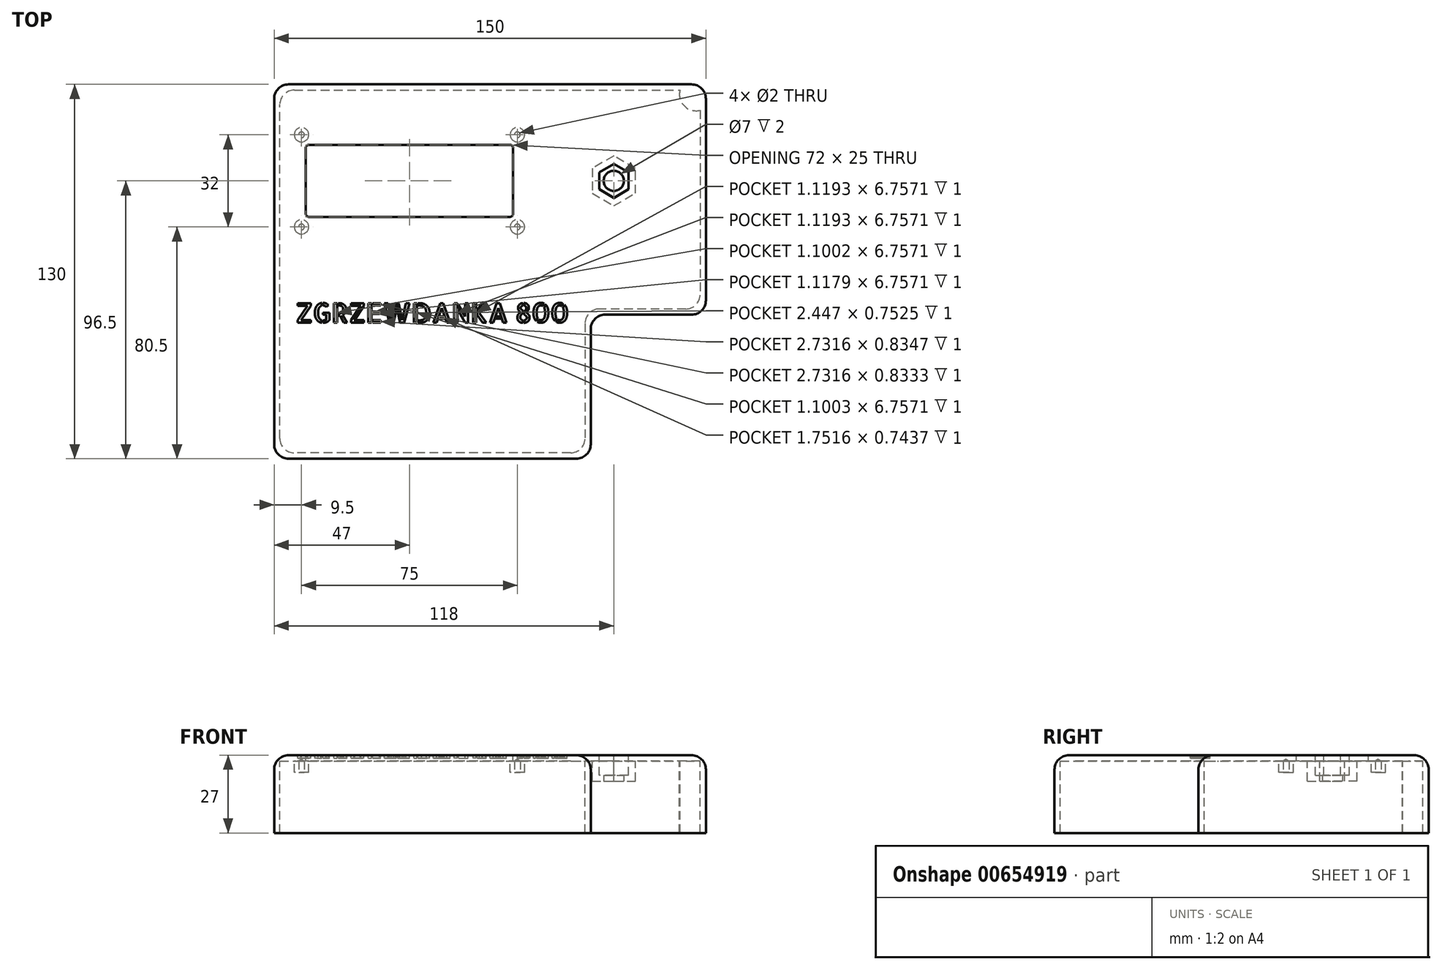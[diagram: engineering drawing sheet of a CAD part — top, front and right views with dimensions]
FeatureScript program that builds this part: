
annotation { "Feature Type Name" : "Feature", "Feature Type Description" : "" }
export const myFeature = defineFeature(function(context is Context, id is Id, definition is map)
    precondition{}
    {
        {
            var Q0;
            Q0=qCreatedBy(makeId("Top.planeOp"),FACE);
            var sketch = newSketch(context, id + "F0", { "sketchPlane" : qUnion([Q0])});
            skLineSegment(sketch, "E0", {"start": v(0, 0) * mm, "end": v(0, 130) * mm});
            skLineSegment(sketch, "E1", {"start": v(0, 130) * mm, "end": v(150, 130) * mm});
            skLineSegment(sketch, "E2", {"start": v(150, 130) * mm, "end": v(150, 50) * mm});
            skLineSegment(sketch, "E3", {"start": v(150, 50) * mm, "end": v(110, 50) * mm});
            skLineSegment(sketch, "E4", {"start": v(110, 50) * mm, "end": v(110, 0) * mm});
            skLineSegment(sketch, "E5", {"start": v(110, 0) * mm, "end": v(0, 0) * mm});
            skSolve(sketch);
        }
        {
            var Q0;
            Q0=makeQuery(id+"F0.imprint","IMPRINT",FACE,{"disambiguationData":[TD([[makeQuery(id+"F0.imprint","IMPRINT",EDGE,{"derivedFrom":sQuery(id+"F0.wireOp",EDGE,"E0")}),-1.0]])]});
            extrude(context, id + "F1", {"entities" : qUnion([Q0]), "depth" : 2 * mm, "offsetDistance" : 25 * mm});
        }
        {
            var Q0;
            Q0=makeQuery(id+"F1.opExtrude","CAP_FACE",FACE,{"disambiguationData":[OSD([sQuery(id+"F0.wireOp",EDGE,"E0"),sQuery(id+"F0.wireOp",EDGE,"E1"),sQuery(id+"F0.wireOp",EDGE,"E2"),sQuery(id+"F0.wireOp",EDGE,"E3"),sQuery(id+"F0.wireOp",EDGE,"E4"),sQuery(id+"F0.wireOp",EDGE,"E5")])],"isStart":false});
            var sketch = newSketch(context, id + "F2", { "sketchPlane" : qUnion([Q0])});
            skLineSegment(sketch, "E6.bottom", {"start": v(11, 109) * mm, "end": v(83, 109) * mm});
            skLineSegment(sketch, "E6.top", {"start": v(11, 84) * mm, "end": v(83, 84) * mm});
            skLineSegment(sketch, "E6.left", {"start": v(11, 109) * mm, "end": v(11, 84) * mm});
            skLineSegment(sketch, "E6.right", {"start": v(83, 109) * mm, "end": v(83, 84) * mm});
            skSolve(sketch);
        }
        {
            var Q0;
            Q0 = qSketchRegion(id + "F2", true);
            extrude(context, id + "F3", {"entities" : qUnion([Q0]), "operationType" : NewBodyOperationType.REMOVE, "oppositeDirection" : true, "depth" : 7 * mm, "offsetDistance" : 25 * mm});
        }
        {
            var Q0;
            Q0=makeQuery(id+"F1.opExtrude","CAP_FACE",FACE,{"disambiguationData":[OSD([sQuery(id+"F0.wireOp",EDGE,"E0"),sQuery(id+"F0.wireOp",EDGE,"E1"),sQuery(id+"F0.wireOp",EDGE,"E2"),sQuery(id+"F0.wireOp",EDGE,"E3"),sQuery(id+"F0.wireOp",EDGE,"E4"),sQuery(id+"F0.wireOp",EDGE,"E5")])],"isStart":true});
            var sketch = newSketch(context, id + "F4", { "sketchPlane" : qUnion([Q0])});
            skLineSegment(sketch, "E7", {"start": v(110, 0) * mm, "end": v(0, 0) * mm});
            skLineSegment(sketch, "E8", {"start": v(0, 0) * mm, "end": v(0, -130) * mm});
            skLineSegment(sketch, "E9", {"start": v(0, -130) * mm, "end": v(150, -130) * mm});
            skLineSegment(sketch, "E10", {"start": v(150, -130) * mm, "end": v(150, -50) * mm});
            skLineSegment(sketch, "E11", {"start": v(150, -50) * mm, "end": v(110, -50) * mm});
            skLineSegment(sketch, "E12", {"start": v(110, -50) * mm, "end": v(110, 0) * mm});
            skLineSegment(sketch, "E13", {"start": v(148, -52) * mm, "end": v(108, -52) * mm});
            skLineSegment(sketch, "E14", {"start": v(108, -52) * mm, "end": v(108, -2) * mm});
            skLineSegment(sketch, "E15", {"start": v(108, -2) * mm, "end": v(2, -2) * mm});
            skLineSegment(sketch, "E16", {"start": v(2, -2) * mm, "end": v(2, -128) * mm});
            skLineSegment(sketch, "E17", {"start": v(2, -128) * mm, "end": v(148, -128) * mm});
            skLineSegment(sketch, "E18", {"start": v(148, -128) * mm, "end": v(148, -52) * mm});
            skSolve(sketch);
        }
        {
            var Q0;
            Q0 = qSketchRegion(id + "F4", true);
            extrude(context, id + "F5", {"entities" : qUnion([Q0]), "operationType" : NewBodyOperationType.ADD, "depth" : 25 * mm, "offsetDistance" : 25 * mm});
        }
        {
            var Q0;
            Q0=makeQuery(id+"F5.boolean.opBoolean","MERGE",EDGE,{"derivedFrom":[makeQuery(id+"F1.opExtrude","SWEPT_EDGE",EDGE,{"disambiguationData":[OSD([sQuery(id+"F0.wireOp",EDGE,"E4"),sQuery(id+"F0.wireOp",EDGE,"E5")])]}),makeQuery(id+"F5.opExtrude","SWEPT_EDGE",EDGE,{"disambiguationData":[OSD([sQuery(id+"F4.wireOp",EDGE,"E7"),sQuery(id+"F4.wireOp",EDGE,"E12")])]})]});
            fillet(context, id + "F6", {"entities" : qUnion([Q0]), "radius" : 5 * mm, "tangentPropagation" : true, "allowEdgeOverflow" : false});
        }
        {
            var Q0;
            Q0=makeQuery(id+"F1.opExtrude","CAP_FACE",FACE,{"disambiguationData":[OSD([sQuery(id+"F0.wireOp",EDGE,"E0"),sQuery(id+"F0.wireOp",EDGE,"E1"),sQuery(id+"F0.wireOp",EDGE,"E2"),sQuery(id+"F0.wireOp",EDGE,"E3"),sQuery(id+"F0.wireOp",EDGE,"E4"),sQuery(id+"F0.wireOp",EDGE,"E5")])],"isStart":true});
            var sketch = newSketch(context, id + "F7", { "sketchPlane" : qUnion([Q0])});
            skPoint(sketch, "E19", {"position": v(84.5, -112.5) * mm});
            skPoint(sketch, "E20", {"position": v(84.5, -80.5) * mm});
            skPoint(sketch, "E21", {"position": v(9.5, -112.5) * mm});
            skPoint(sketch, "E22", {"position": v(9.5, -80.5) * mm});
            skCircle(sketch, "E23", {"center": v(84.5, -112.5) * mm, "radius": 2.5 * mm});
            skCircle(sketch, "E24", {"center": v(9.5, -112.5) * mm, "radius": 2.5 * mm});
            skCircle(sketch, "E25", {"center": v(9.5, -80.5) * mm, "radius": 2.5 * mm});
            skCircle(sketch, "E26", {"center": v(84.5, -80.5) * mm, "radius": 2.5 * mm});
            skLineSegment(sketch, "E27", {"start": v(11, -96.5) * mm, "end": v(83, -96.5) * mm});
            skLineSegment(sketch, "E28", {"start": v(47, -109) * mm, "end": v(47, -84) * mm});
            skSolve(sketch);
        }
        {
            var Q0;
            Q0=makeQuery(id+"F3.boolean.opBoolean","COPY",EDGE,{"derivedFrom":makeQuery(id+"F3.opExtrude","SWEPT_EDGE",EDGE,{"disambiguationData":[OSD([sQuery(id+"F2.wireOp",EDGE,"E6.bottom"),sQuery(id+"F2.wireOp",EDGE,"E6.right")])]})});
            var Q1;
            Q1=makeQuery(id+"F3.boolean.opBoolean","COPY",EDGE,{"derivedFrom":makeQuery(id+"F3.opExtrude","SWEPT_EDGE",EDGE,{"disambiguationData":[OSD([sQuery(id+"F2.wireOp",EDGE,"E6.top"),sQuery(id+"F2.wireOp",EDGE,"E6.right")])]})});
            var Q2;
            Q2=makeQuery(id+"F3.boolean.opBoolean","COPY",EDGE,{"derivedFrom":makeQuery(id+"F3.opExtrude","SWEPT_EDGE",EDGE,{"disambiguationData":[OSD([sQuery(id+"F2.wireOp",EDGE,"E6.top"),sQuery(id+"F2.wireOp",EDGE,"E6.left")])]})});
            var Q3;
            Q3=makeQuery(id+"F3.boolean.opBoolean","COPY",EDGE,{"derivedFrom":makeQuery(id+"F3.opExtrude","SWEPT_EDGE",EDGE,{"disambiguationData":[OSD([sQuery(id+"F2.wireOp",EDGE,"E6.bottom"),sQuery(id+"F2.wireOp",EDGE,"E6.left")])]})});
            fillet(context, id + "F8", {"entities" : qUnion([Q0, Q1, Q2, Q3]), "radius" : 1 * mm, "tangentPropagation" : true, "allowEdgeOverflow" : false});
        }
        {
            var Q0;
            Q0=makeQuery(id+"F5.boolean.opBoolean","MERGE",EDGE,{"derivedFrom":[makeQuery(id+"F1.opExtrude","SWEPT_EDGE",EDGE,{"disambiguationData":[OSD([sQuery(id+"F0.wireOp",EDGE,"E0"),sQuery(id+"F0.wireOp",EDGE,"E1")])]}),makeQuery(id+"F5.opExtrude","SWEPT_EDGE",EDGE,{"disambiguationData":[OSD([sQuery(id+"F4.wireOp",EDGE,"E8"),sQuery(id+"F4.wireOp",EDGE,"E9")])]})]});
            var Q1;
            Q1=makeQuery(id+"F5.boolean.opBoolean","MERGE",EDGE,{"derivedFrom":[makeQuery(id+"F1.opExtrude","SWEPT_EDGE",EDGE,{"disambiguationData":[OSD([sQuery(id+"F0.wireOp",EDGE,"E0"),sQuery(id+"F0.wireOp",EDGE,"E5")])]}),makeQuery(id+"F5.opExtrude","SWEPT_EDGE",EDGE,{"disambiguationData":[OSD([sQuery(id+"F4.wireOp",EDGE,"E7"),sQuery(id+"F4.wireOp",EDGE,"E8")])]})]});
            var Q2;
            Q2=makeQuery(id+"F5.boolean.opBoolean","MERGE",EDGE,{"derivedFrom":[makeQuery(id+"F1.opExtrude","SWEPT_EDGE",EDGE,{"disambiguationData":[OSD([sQuery(id+"F0.wireOp",EDGE,"E2"),sQuery(id+"F0.wireOp",EDGE,"E3")])]}),makeQuery(id+"F5.opExtrude","SWEPT_EDGE",EDGE,{"disambiguationData":[OSD([sQuery(id+"F4.wireOp",EDGE,"E10"),sQuery(id+"F4.wireOp",EDGE,"E11")])]})]});
            var Q3;
            Q3=makeQuery(id+"F5.boolean.opBoolean","MERGE",EDGE,{"derivedFrom":[makeQuery(id+"F1.opExtrude","SWEPT_EDGE",EDGE,{"disambiguationData":[OSD([sQuery(id+"F0.wireOp",EDGE,"E3"),sQuery(id+"F0.wireOp",EDGE,"E4")])]}),makeQuery(id+"F5.opExtrude","SWEPT_EDGE",EDGE,{"disambiguationData":[OSD([sQuery(id+"F4.wireOp",EDGE,"E11"),sQuery(id+"F4.wireOp",EDGE,"E12")])]})]});
            var Q4;
            Q4=makeQuery(id+"F5.boolean.opBoolean","MERGE",EDGE,{"derivedFrom":[makeQuery(id+"F1.opExtrude","SWEPT_EDGE",EDGE,{"disambiguationData":[OSD([sQuery(id+"F0.wireOp",EDGE,"E1"),sQuery(id+"F0.wireOp",EDGE,"E2")])]}),makeQuery(id+"F5.opExtrude","SWEPT_EDGE",EDGE,{"disambiguationData":[OSD([sQuery(id+"F4.wireOp",EDGE,"E9"),sQuery(id+"F4.wireOp",EDGE,"E10")])]})]});
            fillet(context, id + "F9", {"entities" : qUnion([Q0, Q1, Q2, Q3, Q4]), "radius" : 5 * mm, "tangentPropagation" : true, "allowEdgeOverflow" : false});
        }
        {
            var Q0;
            Q0=makeQuery(id+"F5.opExtrude","SWEPT_EDGE",EDGE,{"disambiguationData":[OSD([sQuery(id+"F4.wireOp",EDGE,"E13"),sQuery(id+"F4.wireOp",EDGE,"E18")])]});
            var Q1;
            Q1=makeQuery(id+"F5.opExtrude","SWEPT_EDGE",EDGE,{"disambiguationData":[OSD([sQuery(id+"F4.wireOp",EDGE,"E17"),sQuery(id+"F4.wireOp",EDGE,"E18")])]});
            var Q2;
            Q2=makeQuery(id+"F5.opExtrude","SWEPT_EDGE",EDGE,{"disambiguationData":[OSD([sQuery(id+"F4.wireOp",EDGE,"E16"),sQuery(id+"F4.wireOp",EDGE,"E17")])]});
            var Q3;
            Q3=makeQuery(id+"F5.opExtrude","SWEPT_EDGE",EDGE,{"disambiguationData":[OSD([sQuery(id+"F4.wireOp",EDGE,"E14"),sQuery(id+"F4.wireOp",EDGE,"E15")])]});
            var Q4;
            Q4=makeQuery(id+"F5.opExtrude","SWEPT_EDGE",EDGE,{"disambiguationData":[OSD([sQuery(id+"F4.wireOp",EDGE,"E15"),sQuery(id+"F4.wireOp",EDGE,"E16")])]});
            var Q5;
            Q5=makeQuery(id+"F5.opExtrude","SWEPT_EDGE",EDGE,{"disambiguationData":[OSD([sQuery(id+"F4.wireOp",EDGE,"E13"),sQuery(id+"F4.wireOp",EDGE,"E14")])]});
            fillet(context, id + "F10", {"entities" : qUnion([Q0, Q1, Q2, Q3, Q4, Q5]), "radius" : 5 * mm, "tangentPropagation" : true, "allowEdgeOverflow" : false});
        }
        {
            var Q0;
            Q0=makeQuery(id+"F1.opExtrude","CAP_EDGE",EDGE,{"disambiguationData":[OSD([sQuery(id+"F0.wireOp",EDGE,"E0")])],"isStart":false});
            fillet(context, id + "F11", {"entities" : qUnion([Q0]), "radius" : 5 * mm, "tangentPropagation" : true, "allowEdgeOverflow" : false});
        }
        {
            var Q0;
            Q0 = qSketchRegion(id + "F7", true);
            extrude(context, id + "F12", {"entities" : qUnion([Q0]), "operationType" : NewBodyOperationType.ADD, "depth" : 4 * mm, "offsetDistance" : 25 * mm});
        }
        {
            var Q0;
            Q0=makeQuery(id+"F1.opExtrude","CAP_FACE",FACE,{"disambiguationData":[OSD([sQuery(id+"F0.wireOp",EDGE,"E0"),sQuery(id+"F0.wireOp",EDGE,"E1"),sQuery(id+"F0.wireOp",EDGE,"E2"),sQuery(id+"F0.wireOp",EDGE,"E3"),sQuery(id+"F0.wireOp",EDGE,"E4"),sQuery(id+"F0.wireOp",EDGE,"E5")])],"isStart":true});
            var sketch = newSketch(context, id + "F13", { "sketchPlane" : qUnion([Q0])});
            skLineSegment(sketch, "E29", {"start": v(83, -96.5) * mm, "end": v(167.66, -96.5) * mm});
            skPoint(sketch, "E30", {"position": v(118, -96.5) * mm});
            skCircle(sketch, "E31.cCircle", {"center": v(118, -96.5) * mm, "radius": 7.5 * mm, "construction": true});
            skLineSegment(sketch, "E31.0", {"start": v(110.5, -100.83) * mm, "end": v(110.5, -92.17) * mm});
            skLineSegment(sketch, "E31.1", {"start": v(110.5, -92.17) * mm, "end": v(118, -87.84) * mm});
            skLineSegment(sketch, "E31.2", {"start": v(118, -87.84) * mm, "end": v(125.5, -92.17) * mm});
            skLineSegment(sketch, "E31.3", {"start": v(125.5, -92.17) * mm, "end": v(125.5, -100.83) * mm});
            skLineSegment(sketch, "E31.4", {"start": v(125.5, -100.83) * mm, "end": v(118, -105.16) * mm});
            skLineSegment(sketch, "E31.5", {"start": v(118, -105.16) * mm, "end": v(110.5, -100.83) * mm});
            skPoint(sketch, "E31.0.midPoint", {"position": v(110.5, -96.5) * mm});
            skSolve(sketch);
        }
        {
            var Q0;
            Q0 = qSketchRegion(id + "F13", true);
            extrude(context, id + "F14", {"entities" : qUnion([Q0]), "operationType" : NewBodyOperationType.ADD, "depth" : 7 * mm, "offsetDistance" : 25 * mm});
        }
        {
            var Q0;
            Q0=makeQuery(id+"F1.opExtrude","CAP_FACE",FACE,{"disambiguationData":[OSD([sQuery(id+"F0.wireOp",EDGE,"E0"),sQuery(id+"F0.wireOp",EDGE,"E1"),sQuery(id+"F0.wireOp",EDGE,"E2"),sQuery(id+"F0.wireOp",EDGE,"E3"),sQuery(id+"F0.wireOp",EDGE,"E4"),sQuery(id+"F0.wireOp",EDGE,"E5")])],"isStart":true});
            var sketch = newSketch(context, id + "F15", { "sketchPlane" : qUnion([Q0])});
            skLineSegment(sketch, "E32", {"start": v(110.5, -96.5) * mm, "end": v(125.5, -96.5) * mm});
            skCircle(sketch, "E33.cCircle", {"center": v(118, -96.5) * mm, "radius": 5.1 * mm, "construction": true});
            skLineSegment(sketch, "E33.0", {"start": v(123.1, -93.56) * mm, "end": v(123.1, -99.44) * mm});
            skLineSegment(sketch, "E33.1", {"start": v(123.1, -99.44) * mm, "end": v(118, -102.39) * mm});
            skLineSegment(sketch, "E33.2", {"start": v(118, -102.39) * mm, "end": v(112.9, -99.44) * mm});
            skLineSegment(sketch, "E33.3", {"start": v(112.9, -99.44) * mm, "end": v(112.9, -93.56) * mm});
            skLineSegment(sketch, "E33.4", {"start": v(112.9, -93.56) * mm, "end": v(118, -90.61) * mm});
            skLineSegment(sketch, "E33.5", {"start": v(118, -90.61) * mm, "end": v(123.1, -93.56) * mm});
            skPoint(sketch, "E33.0.midPoint", {"position": v(123.1, -96.5) * mm});
            skSolve(sketch);
        }
        {
            var Q0;
            Q0 = qSketchRegion(id + "F15", true);
            extrude(context, id + "F16", {"entities" : qUnion([Q0]), "operationType" : NewBodyOperationType.REMOVE, "depth" : 5 * mm, "offsetDistance" : 25 * mm, "hasSecondDirection" : true, "secondDirectionOppositeDirection" : true, "secondDirectionDepth" : 3 * mm});
        }
        {
            var Q0;
            Q0=makeQuery(id+"F14.opExtrude","CAP_FACE",FACE,{"disambiguationData":[OSD([sQuery(id+"F13.wireOp",EDGE,"E31.0"),sQuery(id+"F13.wireOp",EDGE,"E31.1"),sQuery(id+"F13.wireOp",EDGE,"E31.2"),sQuery(id+"F13.wireOp",EDGE,"E31.3"),sQuery(id+"F13.wireOp",EDGE,"E31.4"),sQuery(id+"F13.wireOp",EDGE,"E31.5")])],"isStart":false});
            var sketch = newSketch(context, id + "F17", { "sketchPlane" : qUnion([Q0])});
            skLineSegment(sketch, "E34", {"start": v(125.5, -96.5) * mm, "end": v(110.5, -96.5) * mm});
            skPoint(sketch, "E35", {"position": v(118, -96.5) * mm});
            skSolve(sketch);
        }
        {
            var Q0;
            Q0=sQuery(id+"F17.wireOp",VERTEX,"E35");
            var Q1;
            Q1=makeQuery(id+"F1.opExtrude","SWEPT_BODY",BODY,{"disambiguationData":[OSD([sQuery(id+"F0.wireOp",EDGE,"E0"),sQuery(id+"F0.wireOp",EDGE,"E1"),sQuery(id+"F0.wireOp",EDGE,"E2"),sQuery(id+"F0.wireOp",EDGE,"E3"),sQuery(id+"F0.wireOp",EDGE,"E4"),sQuery(id+"F0.wireOp",EDGE,"E5")])]});
            hole(context, id + "F18", {"style" : HoleStyle.SIMPLE, "endStyle" : HoleEndStyle.THROUGH, "holeDiameter" : 7 * mm, "majorDiameter" : 5 * mm, "isTappedThrough" : true, "tappedDepth" : 12 * mm, "tapClearance" : 3, "locations" : qUnion([Q0]), "scope" : qUnion([Q1])});
        }
        {
            var Q0;
            Q0=makeQuery(id+"F12.opExtrude","CAP_FACE",FACE,{"disambiguationData":[OSD([sQuery(id+"F7.wireOp",EDGE,"E23")])],"isStart":false});
            var sketch = newSketch(context, id + "F19", { "sketchPlane" : qUnion([Q0])});
            skPoint(sketch, "E36", {"position": v(84.5, -112.5) * mm});
            skSolve(sketch);
        }
        {
            var Q0;
            Q0=makeQuery(id+"F12.opExtrude","CAP_FACE",FACE,{"disambiguationData":[OSD([sQuery(id+"F7.wireOp",EDGE,"E25")])],"isStart":false});
            var sketch = newSketch(context, id + "F20", { "sketchPlane" : qUnion([Q0])});
            skPoint(sketch, "E37", {"position": v(9.5, -80.5) * mm});
            skSolve(sketch);
        }
        {
            var Q0;
            Q0=makeQuery(id+"F12.opExtrude","CAP_FACE",FACE,{"disambiguationData":[OSD([sQuery(id+"F7.wireOp",EDGE,"E26")])],"isStart":false});
            var sketch = newSketch(context, id + "F21", { "sketchPlane" : qUnion([Q0])});
            skPoint(sketch, "E38", {"position": v(84.5, -80.5) * mm});
            skSolve(sketch);
        }
        {
            var Q0;
            Q0=makeQuery(id+"F12.opExtrude","CAP_FACE",FACE,{"disambiguationData":[OSD([sQuery(id+"F7.wireOp",EDGE,"E24")])],"isStart":false});
            var sketch = newSketch(context, id + "F22", { "sketchPlane" : qUnion([Q0])});
            skPoint(sketch, "E39", {"position": v(9.5, -112.5) * mm});
            skSolve(sketch);
        }
        {
            var Q0;
            Q0=sQuery(id+"F22.wireOp",VERTEX,"E39");
            var Q1;
            Q1=sQuery(id+"F20.wireOp",VERTEX,"E37");
            var Q2;
            Q2=sQuery(id+"F21.wireOp",VERTEX,"E38");
            var Q3;
            Q3=sQuery(id+"F19.wireOp",VERTEX,"E36");
            var Q4;
            Q4=makeQuery(id+"F1.opExtrude","SWEPT_BODY",BODY,{"disambiguationData":[OSD([sQuery(id+"F0.wireOp",EDGE,"E0"),sQuery(id+"F0.wireOp",EDGE,"E1"),sQuery(id+"F0.wireOp",EDGE,"E2"),sQuery(id+"F0.wireOp",EDGE,"E3"),sQuery(id+"F0.wireOp",EDGE,"E4"),sQuery(id+"F0.wireOp",EDGE,"E5")])]});
            hole(context, id + "F23", {"style" : HoleStyle.SIMPLE, "endStyle" : HoleEndStyle.BLIND, "holeDiameter" : 2 * mm, "majorDiameter" : 5 * mm, "holeDepth" : 4 * mm, "isTappedThrough" : true, "tappedDepth" : 12 * mm, "tapClearance" : 3, "locations" : qUnion([Q0, Q1, Q2, Q3]), "scope" : qUnion([Q4])});
        }
        {
            var Q0;
            Q0=makeQuery(id+"F2.imprint","IMPRINT",FACE,{"disambiguationData":[TD([[makeQuery(id+"F2.imprint","IMPRINT",EDGE,{"derivedFrom":sQuery(id+"F2.wireOp",EDGE,"E6.bottom")}),1.0]])]});
            var sketch = newSketch(context, id + "F24", { "sketchPlane" : qUnion([Q0])});
            skText(sketch, "E40", { "text": "ZGRZEWDANKA 800", "fontName": "AllertaStencil-Regular.ttf"});
            const initialGuessF24  = {"E40": [0.00749, 0.04725, 1, 0, 0.00676]};
            skSetInitialGuess(sketch, initialGuessF24);
            skSolve(sketch);
        }
        {
            var Q0;
            Q0 = qSketchRegion(id + "F24", true);
            extrude(context, id + "F25", {"entities" : qUnion([Q0]), "operationType" : NewBodyOperationType.REMOVE, "depth" : -1 * mm, "offsetDistance" : 25 * mm});
        }
        {
            var Q0;
            Q0=makeQuery(id+"F1.opExtrude","CAP_FACE",FACE,{"disambiguationData":[OSD([sQuery(id+"F0.wireOp",EDGE,"E0"),sQuery(id+"F0.wireOp",EDGE,"E1"),sQuery(id+"F0.wireOp",EDGE,"E2"),sQuery(id+"F0.wireOp",EDGE,"E3"),sQuery(id+"F0.wireOp",EDGE,"E4"),sQuery(id+"F0.wireOp",EDGE,"E5")])],"isStart":true});
            var sketch = newSketch(context, id + "F26", { "sketchPlane" : qUnion([Q0])});
            skPoint(sketch, "E41", {"position": v(141, -128) * mm});
            skPoint(sketch, "E42", {"position": v(148, -121) * mm});
            skArc(sketch, "E43", {"start": v(148, -121) * mm, "mid": v(142.5, -122.5) * mm, "end": v(141, -128) * mm});
            skLineSegment(sketch, "E44", {"start": v(142.5, -122.5) * mm, "end": v(148.54, -128.54) * mm});
            skPoint(sketch, "E45", {"position": v(145.52, -125.52) * mm});
            skArc(sketch, "E46", {"start": v(141, -128) * mm, "mid": v(147.54, -127.54) * mm, "end": v(148, -121) * mm});
            skSolve(sketch);
        }
        {
            var Q0;
            Q0 = qSketchRegion(id + "F26", true);
            extrude(context, id + "F27", {"entities" : qUnion([Q0]), "operationType" : NewBodyOperationType.ADD, "depth" : 25 * mm, "offsetDistance" : 25 * mm});
        }
    });
